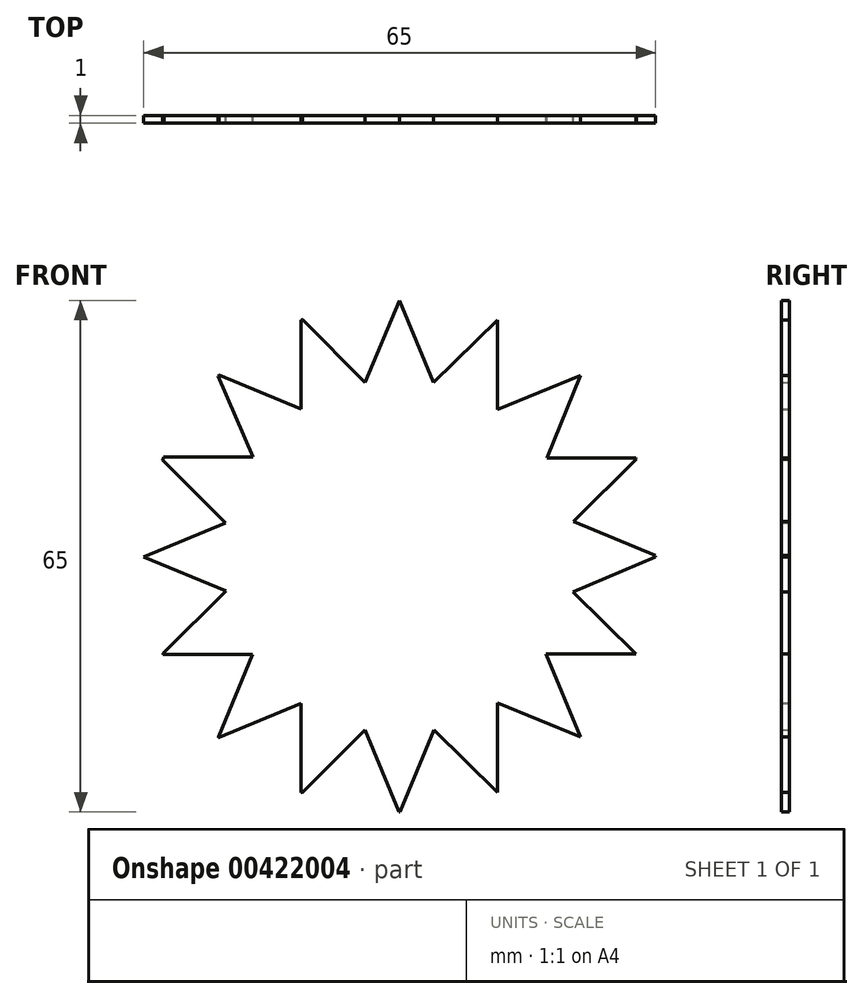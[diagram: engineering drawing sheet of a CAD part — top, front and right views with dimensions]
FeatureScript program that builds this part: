
annotation { "Feature Type Name" : "Feature", "Feature Type Description" : "" }
export const myFeature = defineFeature(function(context is Context, id is Id, definition is map)
    precondition{}
    {
        {
            var Q0;
            Q0=qCreatedBy(makeId("Front.planeOp"),FACE);
            var sketch = newSketch(context, id + "F0", { "sketchPlane" : qUnion([Q0])});
            skCircle(sketch, "E0", {"center": v(0, 0) * mm, "radius": 32.5 * mm});
            skLineSegment(sketch, "E1", {"start": v(0, 32.5) * mm, "end": v(4.32, 22.08) * mm});
            skLineSegment(sketch, "E2", {"start": v(4.32, 22.08) * mm, "end": v(12.44, 30.03) * mm});
            skLineSegment(sketch, "E3", {"start": v(12.44, 30.03) * mm, "end": v(12.44, 18.61) * mm});
            skLineSegment(sketch, "E4", {"start": v(12.44, 18.61) * mm, "end": v(22.98, 22.98) * mm});
            skLineSegment(sketch, "E5", {"start": v(22.98, 22.98) * mm, "end": v(18.7, 12.5) * mm});
            skLineSegment(sketch, "E6", {"start": v(18.7, 12.5) * mm, "end": v(30.18, 12.5) * mm});
            skLineSegment(sketch, "E7", {"start": v(30.18, 12.5) * mm, "end": v(22.07, 4.39) * mm});
            skLineSegment(sketch, "E8", {"start": v(22.07, 4.39) * mm, "end": v(32.66, 0) * mm});
            skLineSegment(sketch, "E9", {"start": v(32.66, 0) * mm, "end": v(22.03, -4.56) * mm});
            skPoint(sketch, "E9.endSnap0", {"position": v(22.92, -4.56) * mm});
            skLineSegment(sketch, "E10", {"start": v(22.03, -4.56) * mm, "end": v(30.03, -12.44) * mm});
            skLineSegment(sketch, "E11", {"start": v(30.03, -12.44) * mm, "end": v(18.61, -12.44) * mm});
            skLineSegment(sketch, "E12", {"start": v(18.61, -12.44) * mm, "end": v(22.98, -22.98) * mm});
            skLineSegment(sketch, "E13", {"start": v(22.98, -22.98) * mm, "end": v(12.44, -18.61) * mm});
            skLineSegment(sketch, "E14", {"start": v(12.44, -18.61) * mm, "end": v(12.44, -30.03) * mm});
            skLineSegment(sketch, "E15", {"start": v(12.44, -30.03) * mm, "end": v(4.39, -22.07) * mm});
            skLineSegment(sketch, "E16", {"start": v(4.39, -22.07) * mm, "end": v(0, -32.66) * mm});
            skLineSegment(sketch, "E17", {"start": v(0, -32.66) * mm, "end": v(-4.39, -22.07) * mm});
            skLineSegment(sketch, "E18", {"start": v(-4.39, -22.07) * mm, "end": v(-12.5, -30.18) * mm});
            skLineSegment(sketch, "E19", {"start": v(-12.5, -30.18) * mm, "end": v(-12.5, -18.7) * mm});
            skLineSegment(sketch, "E20", {"start": v(-12.5, -18.7) * mm, "end": v(-23.1, -23.1) * mm});
            skLineSegment(sketch, "E21", {"start": v(-23.1, -23.1) * mm, "end": v(-18.7, -12.5) * mm});
            skLineSegment(sketch, "E22", {"start": v(-18.7, -12.5) * mm, "end": v(-30.18, -12.5) * mm});
            skLineSegment(sketch, "E23", {"start": v(-30.18, -12.5) * mm, "end": v(-22.07, -4.39) * mm});
            skLineSegment(sketch, "E24", {"start": v(-22.07, -4.39) * mm, "end": v(-32.5, -0.07) * mm});
            skLineSegment(sketch, "E25", {"start": v(-32.5, -0.07) * mm, "end": v(-22.1, 4.24) * mm});
            skLineSegment(sketch, "E26", {"start": v(-22.1, 4.24) * mm, "end": v(-30.48, 12.63) * mm});
            skLineSegment(sketch, "E27", {"start": v(-30.48, 12.63) * mm, "end": v(-18.62, 12.63) * mm});
            skLineSegment(sketch, "E28", {"start": v(-18.62, 12.63) * mm, "end": v(-23.13, 23.13) * mm});
            skLineSegment(sketch, "E29", {"start": v(-23.13, 23.13) * mm, "end": v(-12.52, 18.73) * mm});
            skLineSegment(sketch, "E30", {"start": v(-12.52, 18.73) * mm, "end": v(-12.52, 30.21) * mm});
            skLineSegment(sketch, "E31", {"start": v(-12.52, 30.21) * mm, "end": v(-4.37, 22.07) * mm});
            skLineSegment(sketch, "E32", {"start": v(-4.37, 22.07) * mm, "end": v(0, 32.5) * mm});
            skSolve(sketch);
        }
        {
            var Q0;
            Q0=makeQuery(id+"F0.imprint","IMPRINT",FACE,{"disambiguationData":[TD([[makeQuery(id+"F0.imprint","IMPRINT",EDGE,{"derivedFrom":sQuery(id+"F0.wireOp",EDGE,"E1")}),-1.0]])]});
            extrude(context, id + "F1", {"entities" : qUnion([Q0]), "depth" : 1 * mm});
        }
    });
